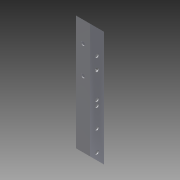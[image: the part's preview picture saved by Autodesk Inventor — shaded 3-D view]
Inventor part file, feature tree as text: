
AUTODESK INVENTOR PART (.ipt)
format: ipt  version: 2013 (Build 170138000, 138)  size: 127,488 bytes
history: native  units: in
note: dims shown in document units (in); Inventor stores cm internally (conversion verified against a paired STEP export)
features: reference x8, extrude x7, sketch x7
ambient origin geometry x8: Origin, YZ Plane, XZ Plane, XY Plane, X Axis, Y Axis, Z Axis, Center Point
bodies: Solid1 (feature_tree)
feature tree (22):
  extrude  "Extrusion1"  Depth=1.0in
  extrude  "Extrusion2"  Depth=10.0in TaperAngle=0.0deg
  extrude  "Extrusion3"  Depth=1.0in TaperAngle=0.0deg
  extrude  "Extrusion4"  Depth=1.0in TaperAngle=0.0deg
  extrude  "Extrusion5"  Depth=0.75in
  extrude  "Extrusion6"  Depth=1.0in TaperAngle=0.0deg
  extrude  "Extrusion7"  [1 undecoded]
  sketch  "Sketch1"  dims[d0=1.0in d2=1.0in]
  sketch  "Sketch2"  dims[d3=0.0625in d4=10.0in d5=0.0in]
  sketch  "Sketch3"  dims[d6=1.0in d7=1.0in d8=0.0in]
  sketch  "Sketch4"  dims[d9=1.0in d10=0.0in d11=1.0in d12=0.0in]
  reference  "Reference1"
  reference  "Reference2"
  sketch  "Sketch5"  dims[d13=1.0in d14=0.75in]
  reference  "Reference3"
  reference  "Reference4"
  sketch  "Sketch6"  dims[d15=1.0in d16=0.0in d17=1.0in d18=0.0in]
  reference  "Reference5"
  reference  "Reference6"
  sketch  "Sketch7"  dims[d19=1.0in d20=0.0in]
  reference  "Reference7"
  reference  "Reference8"
note: 1 required parameter value undecoded (feature->parameter linkage not recoverable at this tier; creation-order binding heuristic only, values carry confidence <= 0.55)
